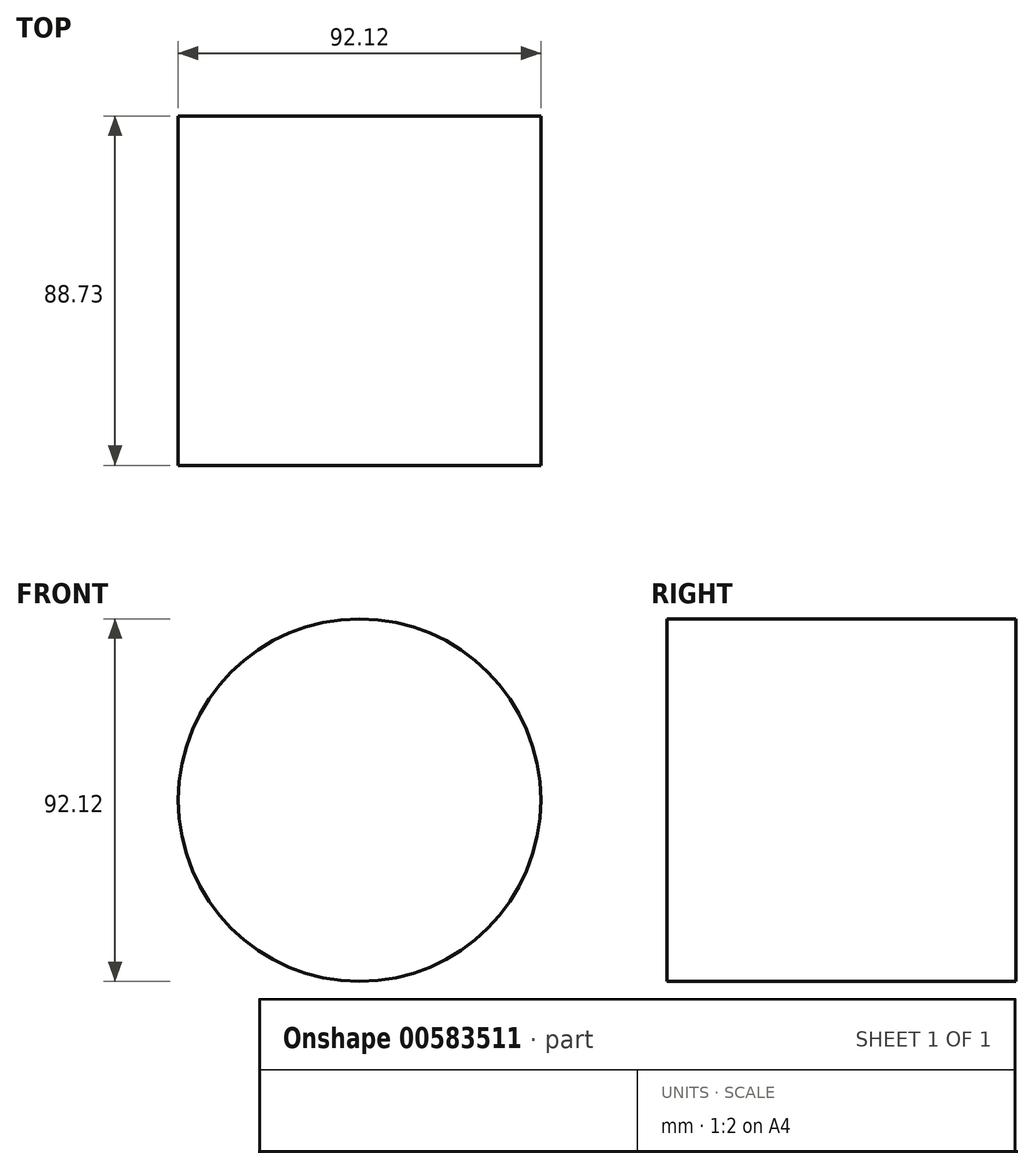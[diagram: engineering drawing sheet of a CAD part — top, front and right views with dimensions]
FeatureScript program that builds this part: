
annotation { "Feature Type Name" : "Feature", "Feature Type Description" : "" }
export const myFeature = defineFeature(function(context is Context, id is Id, definition is map)
    precondition{}
    {
        {
            var Q0;
            Q0=qCreatedBy(makeId("Front.planeOp"),FACE);
            var sketch = newSketch(context, id + "F0", { "sketchPlane" : qUnion([Q0])});
            skCircle(sketch, "E0", {"center": v(0, 0) * mm, "radius": 46.06 * mm});
            skSolve(sketch);
        }
        {
            var Q0;
            Q0=makeQuery(id+"F0.imprint","IMPRINT",FACE,{"disambiguationData":[TD([[makeQuery(id+"F0.imprint","IMPRINT",EDGE,{"derivedFrom":sQuery(id+"F0.wireOp",EDGE,"E0")}),1.0]])]});
            extrude(context, id + "F1", {"entities" : qUnion([Q0]), "depth" : 88.73 * mm, "offsetDistance" : 25.4 * mm});
        }
    });
